# Revit family: Metal_Lockers-Salsbury_Industries-S_66000_Series-Bridge_Unit
name_source: partatom
category: Specialty Equipment
revit_build: Autodesk Revit 2016 (Build: 20150714_1515(x64)
units: mm (PartAtom-declared; Revit-internal decimal feet)

## family parameters
Always vertical = Yes
Cut with Voids When Loaded = No
OmniClass Number = 23.40.00.00
OmniClass Title = Equipment and Furnishings
Part Type = Normal
Room Calculation Point = No
Round Connector Dimension = Use Diameter
Shared = No
Work Plane-Based = No

## types (3) — shared parameters
Assembly Code = C1030310
Depth = 18.01 "
Door Location D1 = See-Through Metal Locker Doors-12 inch with Latch Hasps : Six Tier Door - 6 foot
Hasp Handle Material = Plastic - Salsbury Finish - Black
Hasp Plate Rivet Material = Steel -Salsbury Finish - Polished Steel
Height = 72 "
Manufacturer = Salsbury Industries
MasterFormat Number = 10 51 13
MasterFormat Title = Lockers
OmniClass 23 Number = 23.40.00.00
OmniClass 23 Title = Equipment and Furnishings
Sloping Hood Height = 10.739 "
Type Comments = See-Through Metal Lockers - Six Tier Box Style Bridge
URL = www.lockers.com
Version = 1.0 (03/30/18)
Width = 72.04 "
Window Panel Material = Polycarbonate - Salsbury Finish - Clear
Zee Base - Left Side = Metal Locker Zee Base-Left Side : None
Zee Base - Right Side = Metal Locker Zee Base-Right Side : None
Zee Base Corner - Left Side = Metal Locker Zee Base Corner : None
Zee Base Corner - Right Side3 = Metal Locker Zee Base Corner : None

## per-type parameters (varying)
| type | Base Height | Description | Model | Standard Leg Base | Zee Base |
| S-66016- with Standard 6" High Legs | 6 " | 6 Feet High - 18 Inches Deep | S-66016 | Metal Locker Legs : 6" High - 12"W x 18"D - Bridge | Metal Locker Zee Base : None |
| S-66016 - with 77550 Lockers without Legs | 0 " | 6 Feet High - 18 Inches Deep | S-66016 with 77550 | Metal Locker Legs : No Legs | Metal Locker Zee Base : None |
| S-66016 - with 77578 Zee Base and 77550 Lockers without Legs | 4 " | 6 Feet High - 18 Inches Deep with Zee Base and Lockers without Legs | S-66016 with 77578 and 77550 | Metal Locker Legs : No Legs | Metal Locker Zee Base : 77578 - 12"W x 18" D (Bridge) |

## geometry (parser evidence)
native form markers: Sweep x44
no freeform markers — native parametric forms only
